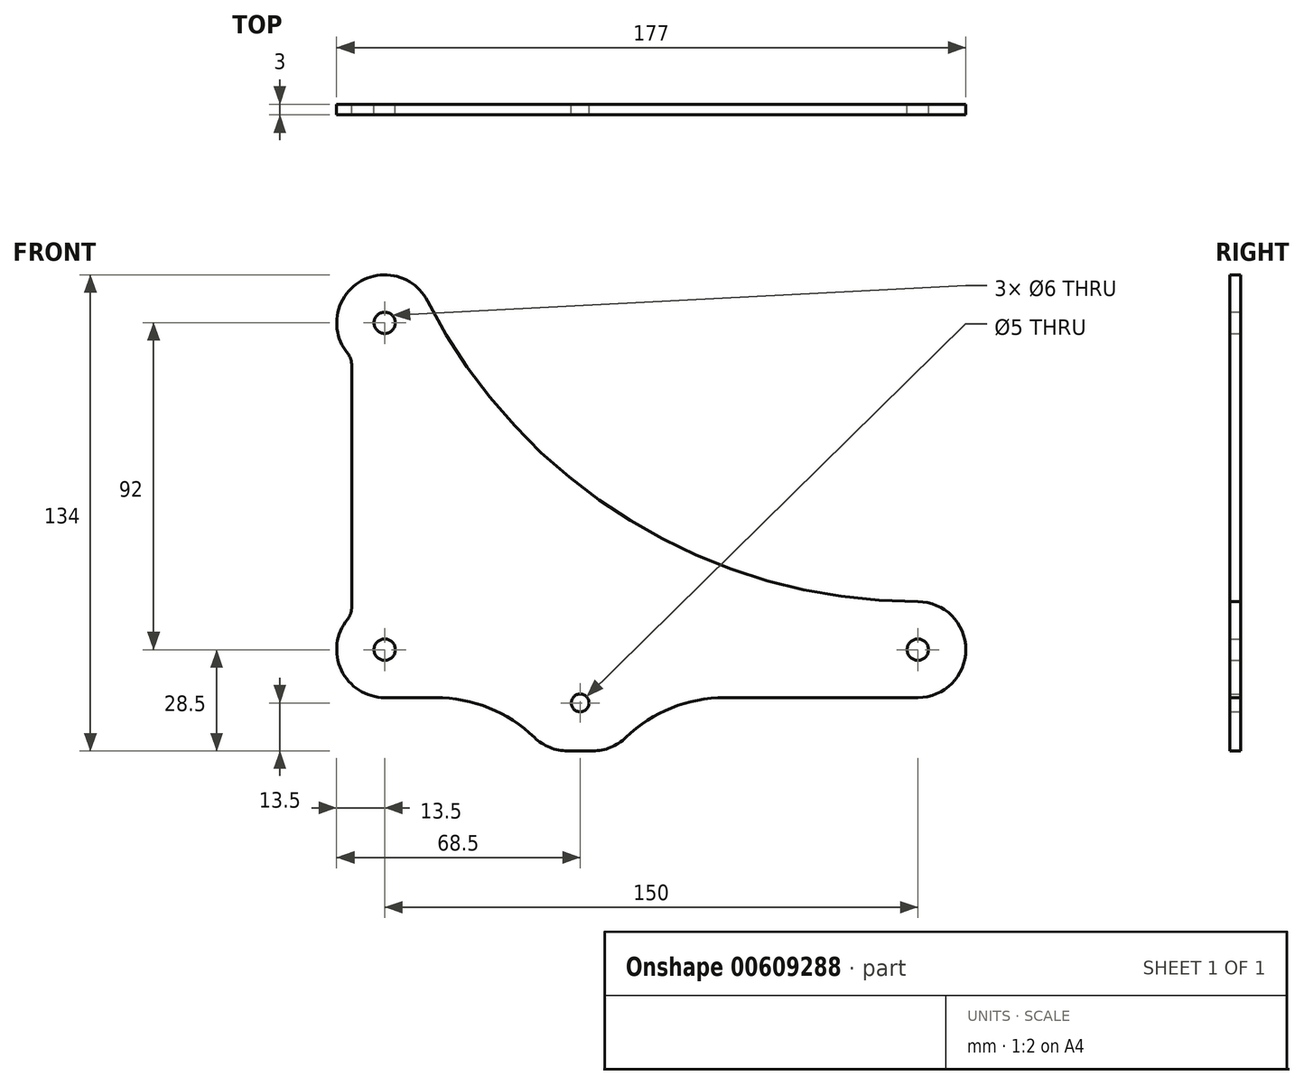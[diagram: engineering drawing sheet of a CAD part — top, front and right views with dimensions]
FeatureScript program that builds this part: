
annotation { "Feature Type Name" : "Feature", "Feature Type Description" : "" }
export const myFeature = defineFeature(function(context is Context, id is Id, definition is map)
    precondition{}
    {
        {
            var Q0;
            Q0=qCreatedBy(makeId("Front.planeOp"),FACE);
            var sketch = newSketch(context, id + "F0", { "sketchPlane" : qUnion([Q0])});
            skCircle(sketch, "E0", {"center": v(0, 0) * mm, "radius": 3 * mm});
            skCircle(sketch, "E1", {"center": v(150, 0) * mm, "radius": 3 * mm});
            skCircle(sketch, "E2", {"center": v(0, 92) * mm, "radius": 3 * mm});
            skCircle(sketch, "E3", {"center": v(55, -15) * mm, "radius": 2.5 * mm});
            skArc(sketch, "E4", {"start": v(-10.44, 8.56) * mm, "mid": v(-12.2, -5.77) * mm, "end": v(0, -13.5) * mm});
            skArc(sketch, "E5", {"start": v(12.03, 98.12) * mm, "mid": v(-7.39, 103.3) * mm, "end": v(-10.44, 83.44) * mm});
            skArc(sketch, "E6", {"start": v(150, -13.5) * mm, "mid": v(163.5, 0) * mm, "end": v(150, 13.5) * mm});
            skLineSegment(sketch, "E7", {"start": v(-9.3, 80.26) * mm, "end": v(-9.3, 11.74) * mm});
            skArc(sketch, "E8", {"start": v(12.03, 98.12) * mm, "mid": v(69.08, 36.34) * mm, "end": v(150, 13.5) * mm});
            skLineSegment(sketch, "E9", {"start": v(150, -13.5) * mm, "end": v(95.65, -13.5) * mm});
            skLineSegment(sketch, "E10", {"start": v(51.5, -15) * mm, "end": v(58.5, -15) * mm, "construction": true});
            skArc(sketch, "E11.0.startCap", {"start": v(51.5, -28.5) * mm, "mid": v(46.45, -27.52) * mm, "end": v(42.13, -24.71) * mm});
            skArc(sketch, "E11.0.endCap", {"start": v(67.87, -24.71) * mm, "mid": v(63.55, -27.52) * mm, "end": v(58.5, -28.5) * mm});
            skLineSegment(sketch, "E11.0.right", {"start": v(51.5, -28.5) * mm, "end": v(58.5, -28.5) * mm});
            skLineSegment(sketch, "E12.trimOffspring", {"start": v(14.35, -13.5) * mm, "end": v(0, -13.5) * mm});
            skPoint(sketch, "E13.visualSharp", {"position": v(-9.3, 82.21) * mm});
            skArc(sketch, "E13.filletArc", {"start": v(-9.3, 80.26) * mm, "mid": v(-9.6, 81.95) * mm, "end": v(-10.44, 83.44) * mm});
            skPoint(sketch, "E14.visualSharp", {"position": v(-9.3, 9.79) * mm});
            skArc(sketch, "E14.filletArc", {"start": v(-10.44, 8.56) * mm, "mid": v(-9.6, 10.05) * mm, "end": v(-9.3, 11.74) * mm});
            skPoint(sketch, "E15.visualSharp", {"position": v(71.92, -13.5) * mm});
            skArc(sketch, "E15.filletArc", {"start": v(95.65, -13.5) * mm, "mid": v(80.67, -16.4) * mm, "end": v(67.87, -24.71) * mm});
            skPoint(sketch, "E16.visualSharp", {"position": v(38.08, -13.5) * mm});
            skArc(sketch, "E16.filletArc", {"start": v(42.13, -24.71) * mm, "mid": v(29.33, -16.4) * mm, "end": v(14.35, -13.5) * mm});
            skSolve(sketch);
        }
        {
            var Q0;
            Q0 = qSketchRegion(id + "F0", true);
            extrude(context, id + "F1", {"entities" : qUnion([Q0]), "depth" : 3 * mm, "offsetDistance" : 25 * mm});
        }
    });
